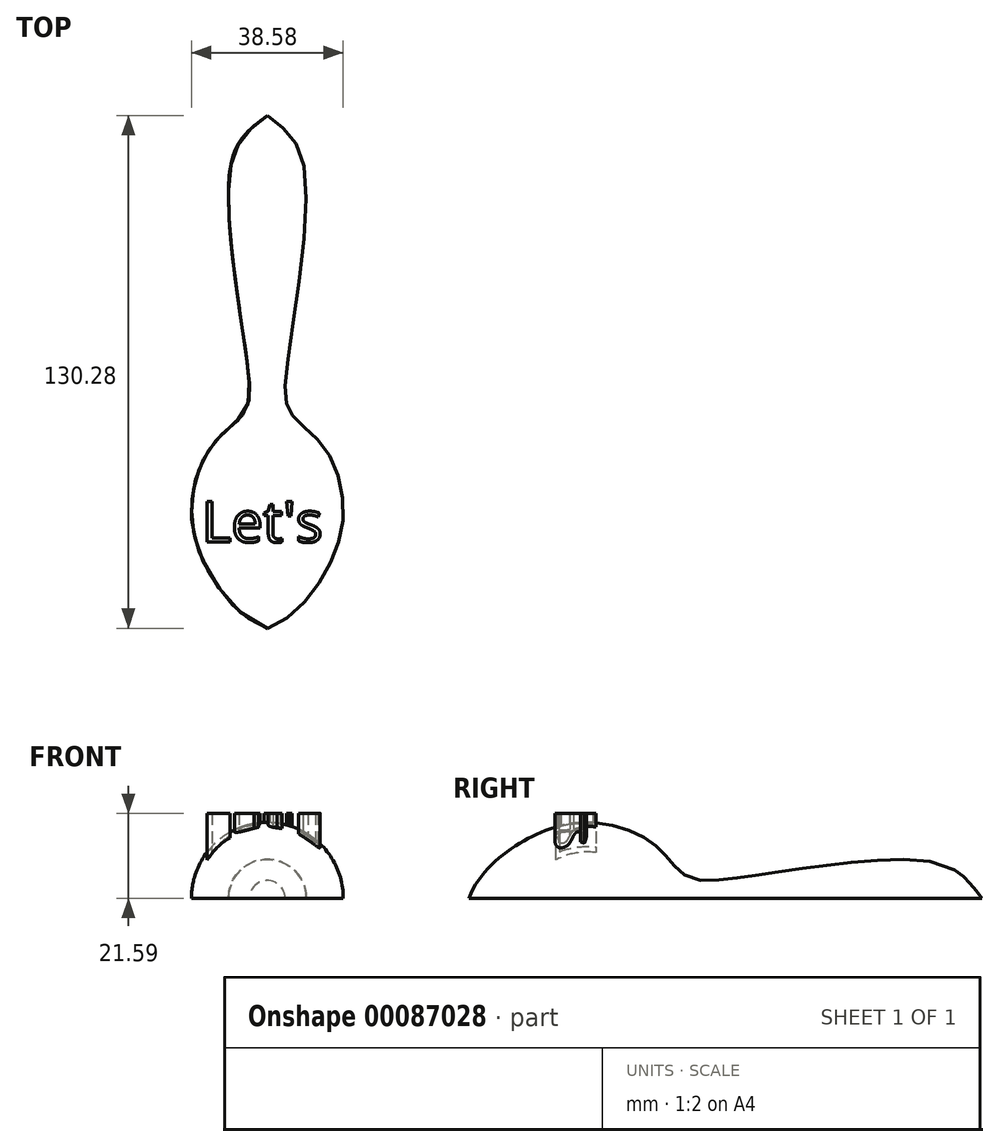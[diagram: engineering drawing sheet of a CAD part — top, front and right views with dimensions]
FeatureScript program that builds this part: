
annotation { "Feature Type Name" : "Feature", "Feature Type Description" : "" }
export const myFeature = defineFeature(function(context is Context, id is Id, definition is map)
    precondition{}
    {
        {
            var Q0;
            Q0=qCreatedBy(makeId("Top.planeOp"),FACE);
            var sketch = newSketch(context, id + "F0", { "sketchPlane" : qUnion([Q0])});
            skFitSpline(sketch, "E0", {"points": [v(0, -65.12) * mm, v(-14.08, -52.12) * mm, v(-19.28, -35.02) * mm, v(-14.08, -18.68) * mm, v(-6.28, -10.87) * mm, v(-4.82, 0) * mm, v(-9.28, 52.54) * mm, v(0, 65.16) * mm], "startDerivative": vector(-121.88, 40.34) * mm, "endDerivative": vector(98.25, 75.03) * mm});
            skLineSegment(sketch, "E1", {"start": v(0, 65.16) * mm, "end": v(0, -65.12) * mm});
            skSolve(sketch);
        }
        {
            var Q0;
            Q0=makeQuery(id+"F0.imprint","IMPRINT",FACE,{"disambiguationData":[TD([[makeQuery(id+"F0.imprint","IMPRINT",EDGE,{"derivedFrom":sQuery(id+"F0.wireOp",EDGE,"E0")}),-1.0]])]});
            extrude(context, id + "F1", {"entities" : qUnion([Q0]), "depth" : 1 / 406.4 * mm});
        }
        {
            var Q0;
            Q0=makeQuery(id+"F1.opExtrude","CAP_FACE",FACE,{"disambiguationData":[OSD([sQuery(id+"F0.wireOp",EDGE,"E0"),sQuery(id+"F0.wireOp",EDGE,"E1")])],"isStart":true});
            var Q1;
            Q1=makeQuery(id+"F1.opExtrude","CAP_EDGE",EDGE,{"disambiguationData":[OSD([sQuery(id+"F0.wireOp",EDGE,"E1")])],"isStart":true});
            revolve(context, id + "F2", {"operationType" : NewBodyOperationType.ADD, "entities" : qUnion([Q0]), "axis" : qUnion([Q1]), "revolveType" : RevolveType.ONE_DIRECTION, "oppositeDirection" : true, "angle" : 179.97 * degree});
        }
        {
            var Q0;
            Q0=qCreatedBy(makeId("Top.planeOp"),FACE);
            var sketch = newSketch(context, id + "F3", { "sketchPlane" : qUnion([Q0])});
            skText(sketch, "E2", { "text": "Let\'s\n", "fontName": "OpenSans-Regular.ttf"});
            const initialGuessF3  = {"E2": [-0.0167, -0.04322, 1, 0, 0.0104]};
            skSetInitialGuess(sketch, initialGuessF3);
            skSolve(sketch);
        }
        {
            var Q0;
            Q0 = qSketchRegion(id + "F3", true);
            extrude(context, id + "F4", {"entities" : qUnion([Q0]), "operationType" : NewBodyOperationType.ADD, "depth" : 21.59 * mm});
        }
    });
